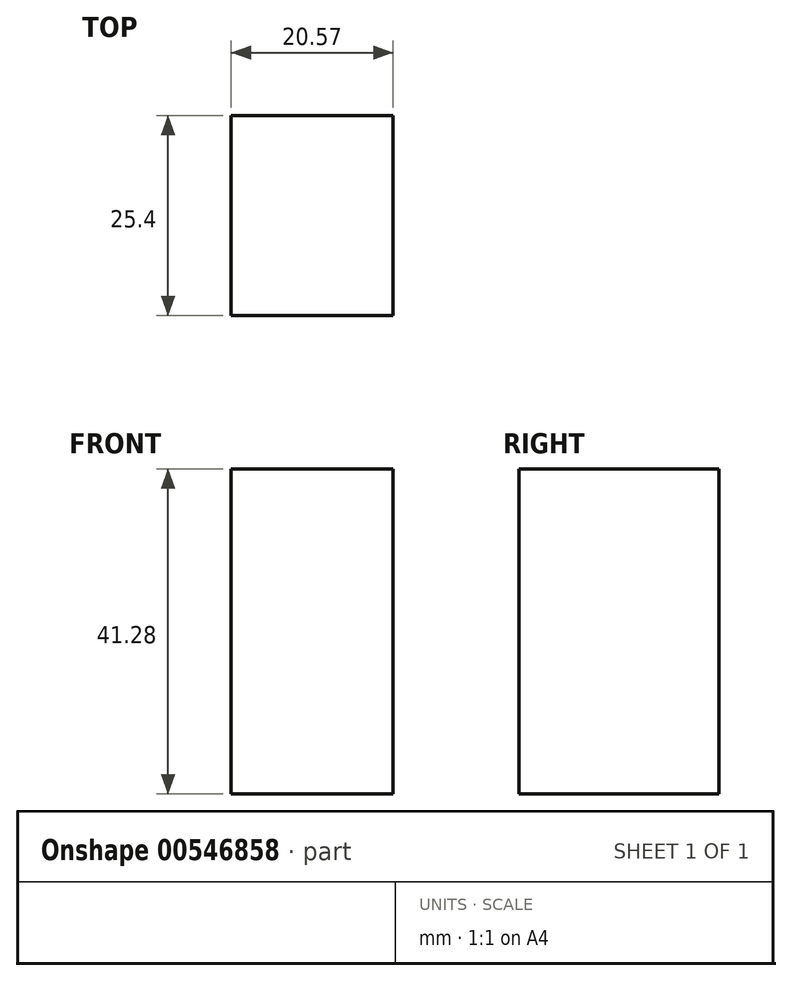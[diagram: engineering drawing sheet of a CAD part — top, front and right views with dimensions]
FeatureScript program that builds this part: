
annotation { "Feature Type Name" : "Feature", "Feature Type Description" : "" }
export const myFeature = defineFeature(function(context is Context, id is Id, definition is map)
    precondition{}
    {
        {
            var Q0;
            Q0=qCreatedBy(makeId("Front.planeOp"),FACE);
            var sketch = newSketch(context, id + "F0", { "sketchPlane" : qUnion([Q0])});
            skLineSegment(sketch, "E0.bottom", {"start": v(-104.87, 63.88) * mm, "end": v(-84.3, 63.88) * mm});
            skLineSegment(sketch, "E0.top", {"start": v(-104.87, 22.6) * mm, "end": v(-84.3, 22.6) * mm});
            skLineSegment(sketch, "E0.left", {"start": v(-104.87, 63.88) * mm, "end": v(-104.87, 22.6) * mm});
            skLineSegment(sketch, "E0.right", {"start": v(-84.3, 63.88) * mm, "end": v(-84.3, 22.6) * mm});
            skSolve(sketch);
        }
        {
            var Q0;
            Q0 = qSketchRegion(id + "F0", true);
            extrude(context, id + "F1", {"entities" : qUnion([Q0]), "depth" : 25.4 * mm, "offsetDistance" : 25.4 * mm});
        }
    });
